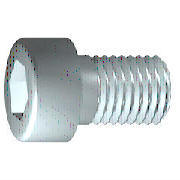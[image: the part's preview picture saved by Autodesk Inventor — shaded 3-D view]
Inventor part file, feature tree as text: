
AUTODESK INVENTOR PART (.ipt)
format: ipt  version: 2020 (Build 240168000, 168)  size: 189,952 bytes
history: native  units: mm (DEFAULTED — no unit token found)
features: sketch x2, other x1, extrude x1, plane x1, fillet x1
ambient origin geometry x7: Origin, YZ Plane, XY Plane, X Axis, Y Axis, Z Axis, Center Point
bodies: Solid1 (feature_tree)
feature tree (6):
  other  "Bryła"
  extrude  "Szczelina"  Depth=16.5mm
  plane  "Work Plane1"
  fillet  "Fillet2"  Radius=0.306825mm
  sketch  "Szkic1"
  sketch  "Szkic2"
